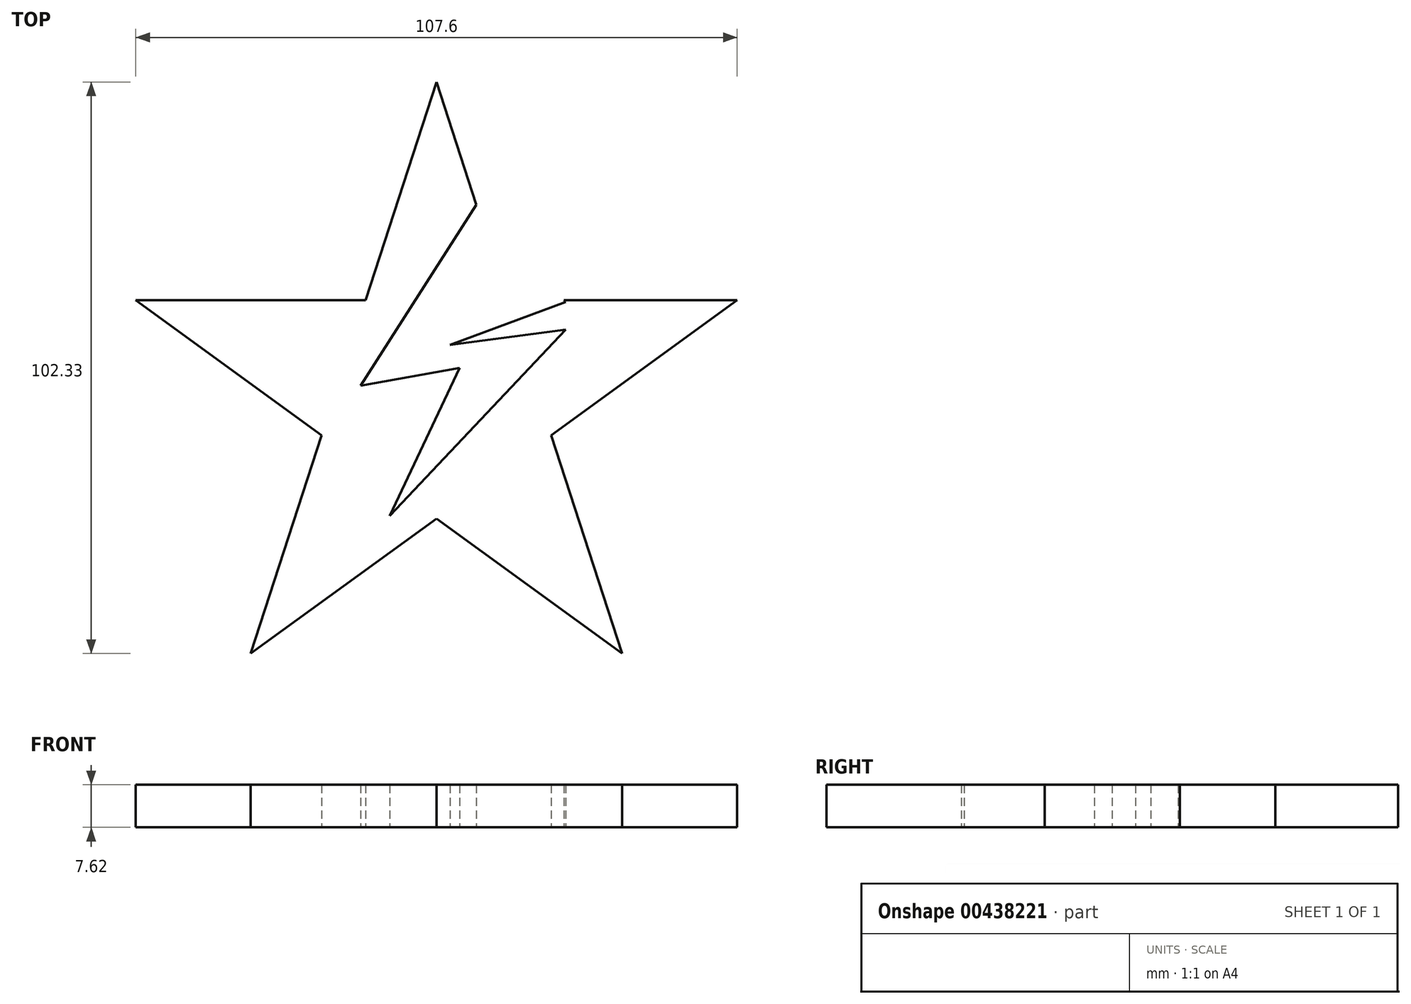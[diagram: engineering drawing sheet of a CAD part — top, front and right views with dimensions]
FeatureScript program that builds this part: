
annotation { "Feature Type Name" : "Feature", "Feature Type Description" : "" }
export const myFeature = defineFeature(function(context is Context, id is Id, definition is map)
    precondition{}
    {
        {
            var Q0;
            Q0=qCreatedBy(makeId("Top.planeOp"),FACE);
            var sketch = newSketch(context, id + "F0", { "sketchPlane" : qUnion([Q0])});
            skCircle(sketch, "E0.cCircle", {"center": v(0, 0) * mm, "radius": 17.48 * mm, "construction": true});
            skLineSegment(sketch, "E0.0", {"start": v(-12.7, 17.48) * mm, "end": v(12.7, 17.48) * mm});
            skLineSegment(sketch, "E0.1", {"start": v(12.7, 17.48) * mm, "end": v(20.55, -6.68) * mm});
            skLineSegment(sketch, "E0.2", {"start": v(20.55, -6.68) * mm, "end": v(0, -21.6) * mm});
            skLineSegment(sketch, "E0.3", {"start": v(0, -21.6) * mm, "end": v(-20.55, -6.68) * mm});
            skLineSegment(sketch, "E0.4", {"start": v(-20.55, -6.68) * mm, "end": v(-12.7, 17.48) * mm});
            skPoint(sketch, "E0.0.midPoint", {"position": v(0, 17.48) * mm});
            skLineSegment(sketch, "E1", {"start": v(-12.7, 17.48) * mm, "end": v(0, 56.57) * mm});
            skLineSegment(sketch, "E2", {"start": v(0, 56.57) * mm, "end": v(12.7, 17.48) * mm});
            skLineSegment(sketch, "E3", {"start": v(12.7, 17.48) * mm, "end": v(53.8, 17.48) * mm});
            skLineSegment(sketch, "E4", {"start": v(53.8, 17.48) * mm, "end": v(20.55, -6.68) * mm});
            skLineSegment(sketch, "E5", {"start": v(20.55, -6.68) * mm, "end": v(33.25, -45.76) * mm});
            skLineSegment(sketch, "E6", {"start": v(0, -21.6) * mm, "end": v(33.25, -45.76) * mm});
            skLineSegment(sketch, "E7", {"start": v(0, -21.6) * mm, "end": v(-33.25, -45.76) * mm});
            skLineSegment(sketch, "E8", {"start": v(-20.55, -6.68) * mm, "end": v(-33.25, -45.76) * mm});
            skLineSegment(sketch, "E9", {"start": v(-20.55, -6.68) * mm, "end": v(-53.8, 17.48) * mm});
            skLineSegment(sketch, "E10", {"start": v(-12.7, 17.48) * mm, "end": v(-53.8, 17.48) * mm});
            skSolve(sketch);
        }
        {
            var Q0;
            Q0 = qSketchRegion(id + "F0", true);
            extrude(context, id + "F1", {"entities" : qUnion([Q0]), "depth" : 7.62 * mm});
        }
        {
            var Q0;
            Q0=qCreatedBy(makeId("Top.planeOp"),FACE);
            var sketch = newSketch(context, id + "F2", { "sketchPlane" : qUnion([Q0])});
            skLineSegment(sketch, "E11", {"start": v(7.3, 34.86) * mm, "end": v(-13.56, 2.2) * mm});
            skLineSegment(sketch, "E12", {"start": v(-13.56, 2.2) * mm, "end": v(4.14, 5.36) * mm});
            skLineSegment(sketch, "E13", {"start": v(4.14, 5.36) * mm, "end": v(-8.38, -21.12) * mm});
            skLineSegment(sketch, "E14", {"start": v(-8.38, -21.12) * mm, "end": v(23.13, 12.26) * mm});
            skLineSegment(sketch, "E15", {"start": v(23.13, 12.26) * mm, "end": v(2.4, 9.53) * mm});
            skLineSegment(sketch, "E16", {"start": v(2.4, 9.53) * mm, "end": v(23.13, 17.16) * mm});
            skLineSegment(sketch, "E17", {"start": v(7.3, 34.86) * mm, "end": v(23.13, 17.16) * mm});
            skSolve(sketch);
        }
        {
            var Q0;
            Q0 = qSketchRegion(id + "F2", true);
            extrude(context, id + "F3", {"entities" : qUnion([Q0]), "operationType" : NewBodyOperationType.REMOVE, "depth" : 25.4 * mm});
        }
    });
